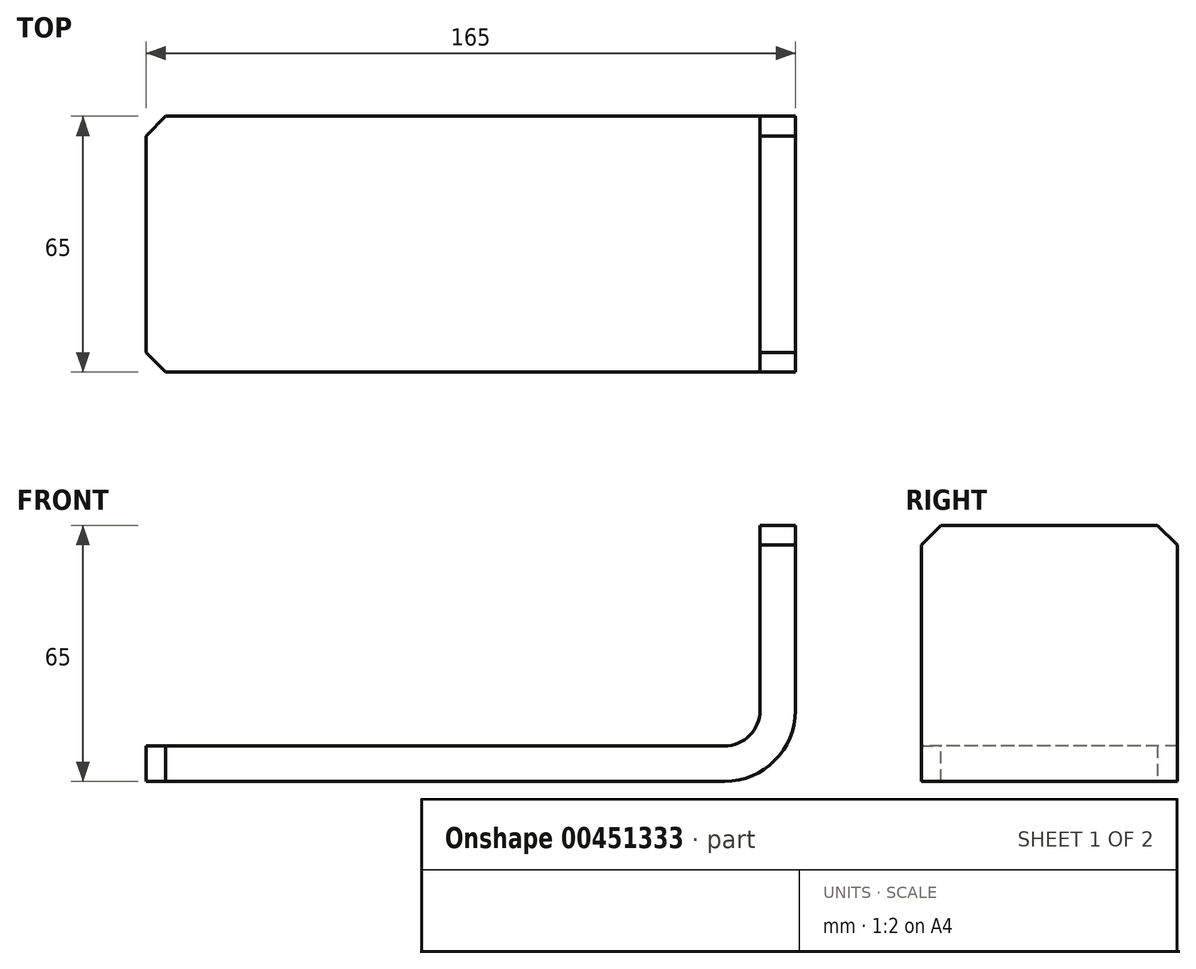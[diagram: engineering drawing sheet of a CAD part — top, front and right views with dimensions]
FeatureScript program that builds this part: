
annotation { "Feature Type Name" : "Feature", "Feature Type Description" : "" }
export const myFeature = defineFeature(function(context is Context, id is Id, definition is map)
    precondition{}
    {
        {
            var Q0;
            Q0=qCreatedBy(makeId("Front.planeOp"),FACE);
            var sketch = newSketch(context, id + "F0", { "sketchPlane" : qUnion([Q0])});
            skLineSegment(sketch, "E0", {"start": v(0, 0) * mm, "end": v(165, 0) * mm});
            skLineSegment(sketch, "E1", {"start": v(165, 0) * mm, "end": v(165, 65) * mm});
            skLineSegment(sketch, "E2", {"start": v(165, 65) * mm, "end": v(156, 65) * mm});
            skLineSegment(sketch, "E3", {"start": v(0, 9) * mm, "end": v(0, 0) * mm});
            skLineSegment(sketch, "E4.0", {"start": v(0, 9) * mm, "end": v(156, 9) * mm});
            skLineSegment(sketch, "E5.0", {"start": v(156, 9) * mm, "end": v(156, 65) * mm});
            skSolve(sketch);
        }
        {
            var Q0;
            Q0=makeQuery(id+"F0.imprint","IMPRINT",FACE,{"disambiguationData":[TD([[makeQuery(id+"F0.imprint","IMPRINT",EDGE,{"derivedFrom":sQuery(id+"F0.wireOp",EDGE,"E0")}),1.0]])]});
            extrude(context, id + "F1", {"entities" : qUnion([Q0]), "oppositeDirection" : true, "depth" : 65 * mm});
        }
        {
            var Q0;
            Q0=makeQuery(id+"F1.opExtrude","SWEPT_EDGE",EDGE,{"disambiguationData":[OSD([sQuery(id+"F0.wireOp",EDGE,"E4.0"),sQuery(id+"F0.wireOp",EDGE,"E5.0")])]});
            fillet(context, id + "F2", {"entities" : qUnion([Q0]), "radius" : 9 * mm, "tangentPropagation" : true, "allowEdgeOverflow" : false});
        }
        {
            var Q0;
            Q0=makeQuery(id+"F1.opExtrude","SWEPT_EDGE",EDGE,{"disambiguationData":[OSD([sQuery(id+"F0.wireOp",EDGE,"E0"),sQuery(id+"F0.wireOp",EDGE,"E1")])]});
            fillet(context, id + "F3", {"entities" : qUnion([Q0]), "radius" : 18 * mm, "tangentPropagation" : true, "allowEdgeOverflow" : false});
        }
        {
            var Q0;
            Q0=makeQuery(id+"F1.opExtrude","CAP_EDGE",EDGE,{"disambiguationData":[OSD([sQuery(id+"F0.wireOp",EDGE,"E2")])],"isStart":false});
            var Q1;
            Q1=makeQuery(id+"F1.opExtrude","CAP_EDGE",EDGE,{"disambiguationData":[OSD([sQuery(id+"F0.wireOp",EDGE,"E2")])],"isStart":true});
            var Q2;
            Q2=makeQuery(id+"F1.opExtrude","CAP_EDGE",EDGE,{"disambiguationData":[OSD([sQuery(id+"F0.wireOp",EDGE,"E3")])],"isStart":false});
            var Q3;
            Q3=makeQuery(id+"F1.opExtrude","CAP_EDGE",EDGE,{"disambiguationData":[OSD([sQuery(id+"F0.wireOp",EDGE,"E3")])],"isStart":true});
            chamfer(context, id + "F4", {"entities" : qUnion([Q0, Q1, Q2, Q3]), "width" : 5 * mm, "tangentPropagation" : true});
        }
    });
